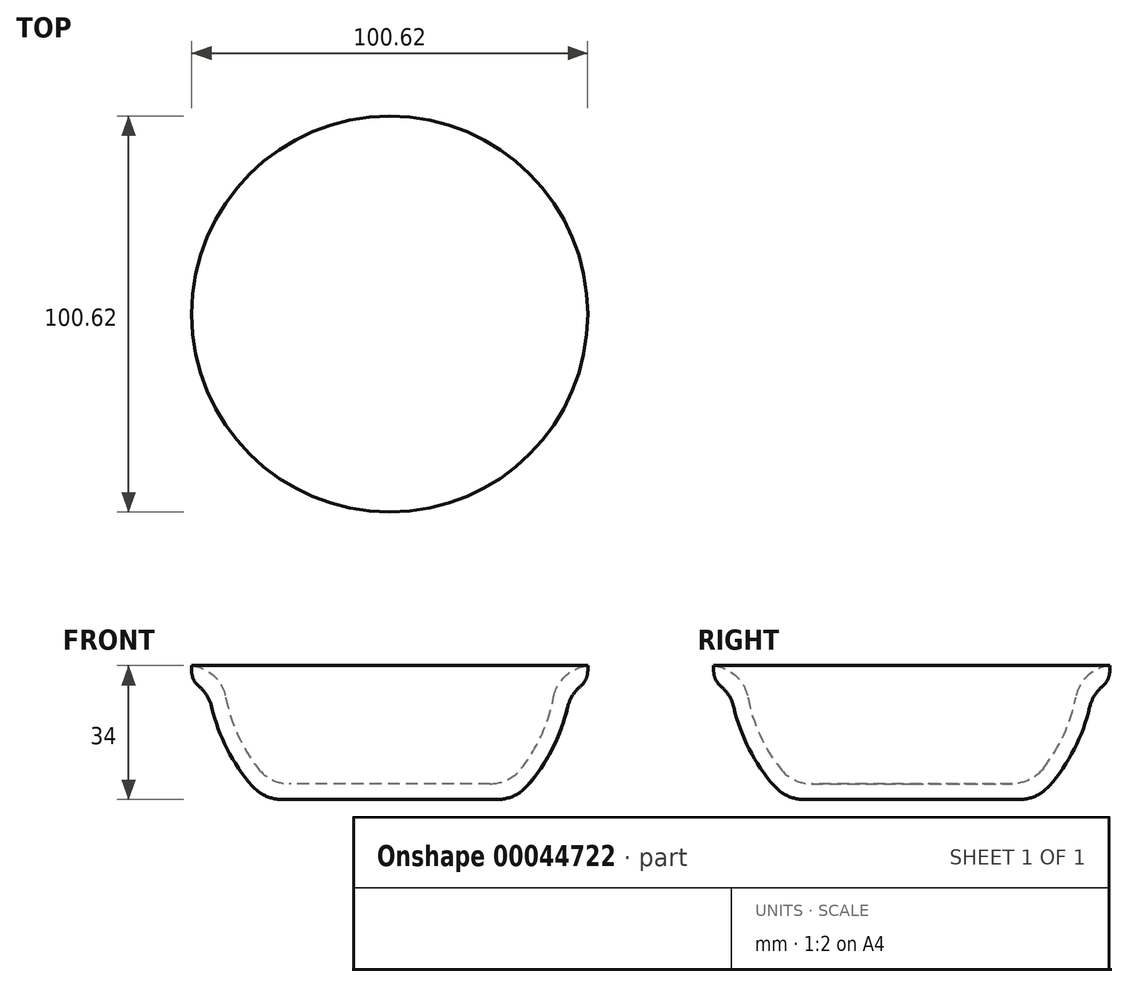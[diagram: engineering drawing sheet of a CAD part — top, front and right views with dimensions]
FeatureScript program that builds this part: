
annotation { "Feature Type Name" : "Feature", "Feature Type Description" : "" }
export const myFeature = defineFeature(function(context is Context, id is Id, definition is map)
    precondition{}
    {
        {
            var Q0;
            Q0=qCreatedBy(makeId("Front.planeOp"),FACE);
            var sketch = newSketch(context, id + "F0", { "sketchPlane" : qUnion([Q0])});
            skLineSegment(sketch, "E0", {"start": v(0, 0) * mm, "end": v(0, -30) * mm});
            skLineSegment(sketch, "E1", {"start": v(0, -30) * mm, "end": v(-30, -30) * mm});
            skArc(sketch, "E2", {"start": v(-30, -30) * mm, "mid": v(-39.2, -16.24) * mm, "end": v(-42.43, 0) * mm});
            skLineSegment(sketch, "E3", {"start": v(-42.43, 0) * mm, "end": v(-50.31, 0) * mm});
            skLineSegment(sketch, "E4.0", {"start": v(-46.25, -4) * mm, "end": v(-50.31, -4) * mm});
            skArc(sketch, "E4.1", {"start": v(-31.61, -34) * mm, "mid": v(-41.72, -20.36) * mm, "end": v(-46.25, -4) * mm});
            skLineSegment(sketch, "E4.2", {"start": v(0, -34) * mm, "end": v(-31.61, -34) * mm});
            skLineSegment(sketch, "E5", {"start": v(-50.31, 0) * mm, "end": v(-50.31, -4) * mm});
            skLineSegment(sketch, "E6", {"start": v(0, -34) * mm, "end": v(0, -30) * mm});
            skSolve(sketch);
        }
        {
            var Q0;
            Q0=makeQuery(id+"F0.imprint","IMPRINT",FACE,{"disambiguationData":[TD([[makeQuery(id+"F0.imprint","IMPRINT",EDGE,{"derivedFrom":sQuery(id+"F0.wireOp",EDGE,"E1")}),1.0]])]});
            var Q1;
            Q1=sQuery(id+"F0.wireOp",EDGE,"E0");
            revolve(context, id + "F1", {"entities" : qUnion([Q0]), "axis" : qUnion([Q1]), "revolveType" : RevolveType.FULL});
        }
        {
            var Q0;
            Q0=makeQuery(id+"F1.opRevolve","SWEPT_EDGE",EDGE,{"disambiguationData":[OSD([sQuery(id+"F0.wireOp",EDGE,"E2"),sQuery(id+"F0.wireOp",EDGE,"E3")])]});
            var Q1;
            Q1=makeQuery(id+"F1.opRevolve","SWEPT_EDGE",EDGE,{"disambiguationData":[OSD([sQuery(id+"F0.wireOp",EDGE,"E1"),sQuery(id+"F0.wireOp",EDGE,"E2")])]});
            var Q2;
            Q2=makeQuery(id+"F1.opRevolve","SWEPT_EDGE",EDGE,{"disambiguationData":[OSD([sQuery(id+"F0.wireOp",EDGE,"E4.0"),sQuery(id+"F0.wireOp",EDGE,"E4.1")])]});
            var Q3;
            Q3=makeQuery(id+"F1.opRevolve","SWEPT_EDGE",EDGE,{"disambiguationData":[OSD([sQuery(id+"F0.wireOp",EDGE,"E4.1"),sQuery(id+"F0.wireOp",EDGE,"E4.2")])]});
            fillet(context, id + "F2", {"entities" : qUnion([Q0, Q1, Q2, Q3]), "radius" : 10 * mm, "tangentPropagation" : true, "allowEdgeOverflow" : false});
        }
        {
            var Q0;
            Q0=makeQuery(id+"F2.opFillet","BLEND_EDGE",EDGE,{"blendedFrom":[makeQuery(id+"F1.opRevolve","SWEPT_EDGE",EDGE,{"disambiguationData":[OSD([sQuery(id+"F0.wireOp",EDGE,"E4.0"),sQuery(id+"F0.wireOp",EDGE,"E4.1")])]}),makeQuery(id+"F1.opRevolve","SWEPT_FACE",FACE,{"disambiguationData":[OSD([sQuery(id+"F0.wireOp",EDGE,"E5")])]})],"blendedInto":[makeQuery(id+"F1.opRevolve","SWEPT_FACE",FACE,{"disambiguationData":[OSD([sQuery(id+"F0.wireOp",EDGE,"E5")])]})]});
            fillet(context, id + "F3", {"entities" : qUnion([Q0]), "radius" : 5 * mm, "tangentPropagation" : true, "allowEdgeOverflow" : false});
        }
    });
